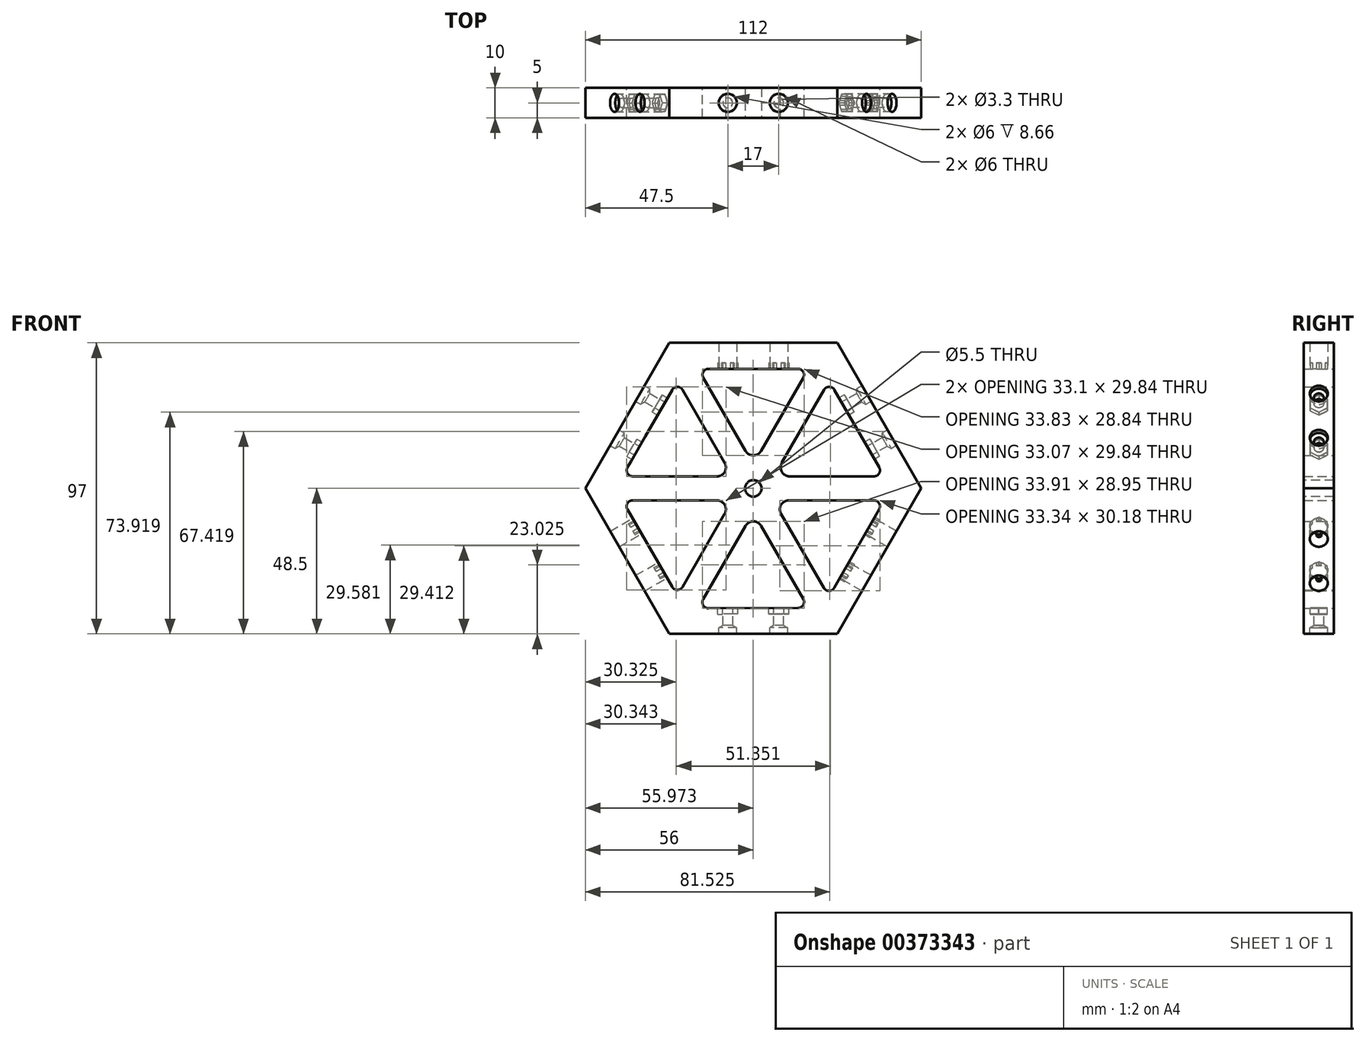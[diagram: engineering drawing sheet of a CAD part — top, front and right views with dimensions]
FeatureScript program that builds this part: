
annotation { "Feature Type Name" : "Feature", "Feature Type Description" : "" }
export const myFeature = defineFeature(function(context is Context, id is Id, definition is map)
    precondition{}
    {
        {
            var Q0;
            Q0=qCreatedBy(makeId("Front.planeOp"),FACE);
            var sketch = newSketch(context, id + "F0", { "sketchPlane" : qUnion([Q0])});
            skCircle(sketch, "E0.cCircle", {"center": v(0, 0) * mm, "radius": 56 * mm, "construction": true});
            skLineSegment(sketch, "E0.0", {"start": v(56, 0) * mm, "end": v(28, -48.5) * mm});
            skLineSegment(sketch, "E0.1", {"start": v(28, -48.5) * mm, "end": v(-28, -48.5) * mm});
            skLineSegment(sketch, "E0.2", {"start": v(-28, -48.5) * mm, "end": v(-56, 0) * mm});
            skLineSegment(sketch, "E0.3", {"start": v(-56, 0) * mm, "end": v(-28, 48.5) * mm});
            skLineSegment(sketch, "E0.4", {"start": v(-28, 48.5) * mm, "end": v(28, 48.5) * mm});
            skLineSegment(sketch, "E0.5", {"start": v(28, 48.5) * mm, "end": v(56, 0) * mm});
            skCircle(sketch, "E1.cCircle", {"center": v(0, 0) * mm, "radius": 46 * mm, "construction": true});
            skLineSegment(sketch, "E1.2", {"start": v(-27.04, -32.84) * mm, "end": v(-41.96, -7) * mm});
            skLineSegment(sketch, "E1.3", {"start": v(-36, 17.34) * mm, "end": v(-27.04, 32.84) * mm});
            skLineSegment(sketch, "E1.4", {"start": v(-14.92, 39.84) * mm, "end": v(14.92, 39.84) * mm});
            skPoint(sketch, "E2.newPointB", {"position": v(-46, 0) * mm});
            skPoint(sketch, "E3.visualSharp", {"position": v(-23, 39.84) * mm});
            skPoint(sketch, "E4.visualSharp", {"position": v(23, 39.84) * mm});
            skPoint(sketch, "E5.newPointA", {"position": v(46, 0) * mm});
            skPoint(sketch, "E6.visualSharp", {"position": v(23, -39.84) * mm});
            skLineSegment(sketch, "E7", {"start": v(-40.71, 9.07) * mm, "end": v(-41.92, 7) * mm});
            skPoint(sketch, "E8.visualSharp", {"position": v(-23, -39.84) * mm});
            skCircle(sketch, "E9", {"center": v(0, 0) * mm, "radius": 4 * mm});
            skLineSegment(sketch, "E10", {"start": v(-36, 17.34) * mm, "end": v(-40.71, 9.07) * mm});
            skLineSegment(sketch, "E11", {"start": v(41.93, -7) * mm, "end": v(26.97, -33.17) * mm});
            skPoint(sketch, "E12.startSnap0", {"position": v(-20.52, 10.54) * mm});
            skPoint(sketch, "E13", {"position": v(40.21, -10) * mm});
            skLineSegment(sketch, "E14", {"start": v(-12.12, 4) * mm, "end": v(-40.2, 4) * mm});
            skLineSegment(sketch, "E15", {"start": v(-12.12, -4) * mm, "end": v(-40.23, -4) * mm});
            skLineSegment(sketch, "E16", {"start": v(12.12, 4) * mm, "end": v(40.23, 4) * mm});
            skLineSegment(sketch, "E17", {"start": v(11.85, -4) * mm, "end": v(40.2, -4) * mm});
            skLineSegment(sketch, "E18", {"start": v(-2.6, 12.5) * mm, "end": v(-16.65, 36.84) * mm});
            skLineSegment(sketch, "E19", {"start": v(-9.53, 8.5) * mm, "end": v(-23.58, 32.84) * mm});
            skLineSegment(sketch, "E20", {"start": v(2.6, 12.5) * mm, "end": v(16.65, 36.84) * mm});
            skLineSegment(sketch, "E21", {"start": v(9.53, 8.5) * mm, "end": v(23.58, 32.84) * mm});
            skLineSegment(sketch, "E22", {"start": v(9.25, -8.5) * mm, "end": v(23.5, -33.18) * mm});
            skLineSegment(sketch, "E23", {"start": v(2.6, -12.5) * mm, "end": v(16.66, -36.85) * mm});
            skPoint(sketch, "E23.endSnap0", {"position": v(16.38, -39.84) * mm});
            skLineSegment(sketch, "E24", {"start": v(-2.6, -12.5) * mm, "end": v(-16.71, -36.95) * mm});
            skLineSegment(sketch, "E25", {"start": v(-9.53, -8.5) * mm, "end": v(-23.58, -32.84) * mm});
            skPoint(sketch, "E26.newPointA", {"position": v(-3.46, 2) * mm});
            skPoint(sketch, "E26.newPointB", {"position": v(3.46, 2) * mm});
            skArc(sketch, "E26.filletArc", {"start": v(-2.6, 12.5) * mm, "mid": v(0, 11) * mm, "end": v(2.6, 12.5) * mm});
            skArc(sketch, "E27.filletArc", {"start": v(9.53, 8.5) * mm, "mid": v(9.53, 5.5) * mm, "end": v(12.12, 4) * mm});
            skArc(sketch, "E28.filletArc", {"start": v(11.85, -4) * mm, "mid": v(9.25, -5.5) * mm, "end": v(9.25, -8.5) * mm});
            skArc(sketch, "E29.filletArc", {"start": v(2.6, -12.5) * mm, "mid": v(0, -11) * mm, "end": v(-2.6, -12.5) * mm});
            skPoint(sketch, "E30.newPointB", {"position": v(0, -4) * mm});
            skArc(sketch, "E30.filletArc", {"start": v(-9.53, -8.5) * mm, "mid": v(-9.53, -5.5) * mm, "end": v(-12.12, -4) * mm});
            skPoint(sketch, "E31.newPointA", {"position": v(0, 4) * mm});
            skArc(sketch, "E31.filletArc", {"start": v(-12.12, 4) * mm, "mid": v(-9.53, 5.5) * mm, "end": v(-9.53, 8.5) * mm});
            skArc(sketch, "E32.filletArc", {"start": v(16.65, 36.84) * mm, "mid": v(16.65, 38.84) * mm, "end": v(14.92, 39.84) * mm});
            skArc(sketch, "E33.filletArc", {"start": v(-23.58, 32.84) * mm, "mid": v(-25.3, 33.84) * mm, "end": v(-27.04, 32.84) * mm});
            skArc(sketch, "E34.filletArc", {"start": v(-14.92, 39.84) * mm, "mid": v(-16.65, 38.84) * mm, "end": v(-16.65, 36.84) * mm});
            skArc(sketch, "E35.filletArc", {"start": v(-41.92, 7) * mm, "mid": v(-41.92, 5) * mm, "end": v(-40.2, 4) * mm});
            skArc(sketch, "E36.filletArc", {"start": v(-40.23, -4) * mm, "mid": v(-41.96, -5) * mm, "end": v(-41.96, -7) * mm});
            skArc(sketch, "E37.filletArc", {"start": v(-27.04, -32.84) * mm, "mid": v(-25.3, -33.84) * mm, "end": v(-23.58, -32.84) * mm});
            skLineSegment(sketch, "E38", {"start": v(12.5, -39.84) * mm, "end": v(-14.97, -39.95) * mm});
            skArc(sketch, "E39.filletArc", {"start": v(-16.71, -36.95) * mm, "mid": v(-16.71, -38.95) * mm, "end": v(-14.97, -39.95) * mm});
            skLineSegment(sketch, "E40", {"start": v(-14.97, -39.95) * mm, "end": v(14.93, -39.85) * mm});
            skArc(sketch, "E41.filletArc", {"start": v(14.93, -39.85) * mm, "mid": v(16.66, -38.85) * mm, "end": v(16.66, -36.85) * mm});
            skArc(sketch, "E42.filletArc", {"start": v(23.5, -33.18) * mm, "mid": v(25.24, -34.18) * mm, "end": v(26.97, -33.17) * mm});
            skArc(sketch, "E43.filletArc", {"start": v(41.93, -7) * mm, "mid": v(41.93, -5) * mm, "end": v(40.2, -4) * mm});
            skArc(sketch, "E44.filletArc", {"start": v(40.23, 4) * mm, "mid": v(41.96, 5) * mm, "end": v(41.96, 7) * mm});
            skPoint(sketch, "E45.visualSharp", {"position": v(25.3, 35.84) * mm});
            skArc(sketch, "E45.filletArc", {"start": v(27.04, 32.84) * mm, "mid": v(25.3, 33.84) * mm, "end": v(23.58, 32.84) * mm});
            skLineSegment(sketch, "E46", {"start": v(27.04, 32.84) * mm, "end": v(41.96, 7) * mm});
            skSolve(sketch);
        }
        {
            var Q0;
            Q0=makeQuery(id+"F0.imprint","IMPRINT",FACE,{"disambiguationData":[TD([[makeQuery(id+"F0.imprint","IMPRINT",EDGE,{"derivedFrom":sQuery(id+"F0.wireOp",EDGE,"E0.0")}),-1.0]])]});
            var Q1;
            Q1=makeQuery(id+"F0.imprint","IMPRINT",FACE,{"disambiguationData":[TD([[makeQuery(id+"F0.imprint","IMPRINT",EDGE,{"derivedFrom":sQuery(id+"F0.wireOp",EDGE,"E9")}),1.0]])]});
            var Q2;
            Q2=makeQuery(id+"F0.imprint","IMPRINT",FACE,{"disambiguationData":[TD([[makeQuery(id+"F0.imprint","IMPRINT",EDGE,{"derivedFrom":sQuery(id+"F0.wireOp",EDGE,"qtYv5Qlg-lz4s-kEUD-Om88-7lSdra8USrlq")}),-1.0]])]});
            extrude(context, id + "F1", {"entities" : qUnion([Q0, Q1, Q2]), "depth" : 3 * mm});
        }
        {
            var Q0;
            Q0=qSketchRegion(id+"F0",true);
            var Q1;
            Q1=makeQuery(id+"F0.imprint","IMPRINT",FACE,{"disambiguationData":[TD([[makeQuery(id+"F0.imprint","IMPRINT",EDGE,{"derivedFrom":sQuery(id+"F0.wireOp",EDGE,"E9")}),1.0]])]});
            extrude(context, id + "F2", {"entities" : qUnion([Q0, Q1]), "operationType" : NewBodyOperationType.ADD, "depth" : 10 * mm});
        }
        {
            var Q0;
            {var subQ0=sQuery(id+"F0.wireOp",EDGE,"E0.1");Q0=makeQuery(id+"F2.boolean.opBoolean","MERGE",FACE,{"derivedFrom":[makeQuery(id+"F1.opExtrude","SWEPT_FACE",FACE,{"disambiguationData":[OSD([subQ0])]}),makeQuery(id+"F2.opExtrude","SWEPT_FACE",FACE,{"disambiguationData":[OSD([subQ0])]})]});}
            var sketch = newSketch(context, id + "F3", { "sketchPlane" : qUnion([Q0])});
            skPoint(sketch, "E47", {"position": v(-8.5, 5) * mm});
            skPoint(sketch, "E48", {"position": v(8.5, 5) * mm});
            skSolve(sketch);
        }
        {
            var Q0;
            {var subQ0=sQuery(id+"F0.wireOp",EDGE,"E0.0");Q0=makeQuery(id+"F2.boolean.opBoolean","MERGE",FACE,{"derivedFrom":[makeQuery(id+"F1.opExtrude","SWEPT_FACE",FACE,{"disambiguationData":[OSD([subQ0])]}),makeQuery(id+"F2.opExtrude","SWEPT_FACE",FACE,{"disambiguationData":[OSD([subQ0])]})]});}
            var sketch = newSketch(context, id + "F4", { "sketchPlane" : qUnion([Q0])});
            skPoint(sketch, "E49", {"position": v(-5, -8.5) * mm});
            skPoint(sketch, "E50", {"position": v(-5, 8.5) * mm});
            skSolve(sketch);
        }
        {
            var Q0;
            {var subQ0=sQuery(id+"F0.wireOp",EDGE,"E0.5");Q0=makeQuery(id+"F2.boolean.opBoolean","MERGE",FACE,{"derivedFrom":[makeQuery(id+"F1.opExtrude","SWEPT_FACE",FACE,{"disambiguationData":[OSD([subQ0])]}),makeQuery(id+"F2.opExtrude","SWEPT_FACE",FACE,{"disambiguationData":[OSD([subQ0])]})]});}
            var sketch = newSketch(context, id + "F5", { "sketchPlane" : qUnion([Q0])});
            skPoint(sketch, "E51", {"position": v(-5, -8.5) * mm});
            skPoint(sketch, "E52", {"position": v(-5, 8.5) * mm});
            skPoint(sketch, "E53.0.midPoint", {"position": v(-2.2, 8.5) * mm});
            skPoint(sketch, "E54.0.midPoint", {"position": v(-2.2, -8.5) * mm});
            skSolve(sketch);
        }
        {
            var Q0;
            {var subQ0=sQuery(id+"F0.wireOp",EDGE,"E0.3");Q0=makeQuery(id+"F2.boolean.opBoolean","MERGE",FACE,{"derivedFrom":[makeQuery(id+"F1.opExtrude","SWEPT_FACE",FACE,{"disambiguationData":[OSD([subQ0])]}),makeQuery(id+"F2.opExtrude","SWEPT_FACE",FACE,{"disambiguationData":[OSD([subQ0])]})]});}
            var sketch = newSketch(context, id + "F6", { "sketchPlane" : qUnion([Q0])});
            skPoint(sketch, "E55.endSnap0", {"position": v(5, 28) * mm});
            skPoint(sketch, "E56", {"position": v(5, 8.5) * mm});
            skPoint(sketch, "E57", {"position": v(5, -8.5) * mm});
            skSolve(sketch);
        }
        {
            var Q0;
            {var subQ0=sQuery(id+"F0.wireOp",EDGE,"E0.2");Q0=makeQuery(id+"F2.boolean.opBoolean","MERGE",FACE,{"derivedFrom":[makeQuery(id+"F1.opExtrude","SWEPT_FACE",FACE,{"disambiguationData":[OSD([subQ0])]}),makeQuery(id+"F2.opExtrude","SWEPT_FACE",FACE,{"disambiguationData":[OSD([subQ0])]})]});}
            var sketch = newSketch(context, id + "F7", { "sketchPlane" : qUnion([Q0])});
            skPoint(sketch, "E58", {"position": v(5, 8.5) * mm});
            skPoint(sketch, "E59", {"position": v(5, -8.5) * mm});
            skSolve(sketch);
        }
        {
            var Q0;
            Q0=sQuery(id+"F3.wireOp",VERTEX,"E47");
            var Q1;
            Q1=sQuery(id+"F3.wireOp",VERTEX,"E48");
            var Q2;
            Q2=makeQuery(id+"F1.opExtrude","SWEPT_BODY",BODY,{"disambiguationData":[OSD([sQuery(id+"F0.wireOp",EDGE,"E0.0"),sQuery(id+"F0.wireOp",EDGE,"E0.1"),sQuery(id+"F0.wireOp",EDGE,"E0.2"),sQuery(id+"F0.wireOp",EDGE,"E0.3"),sQuery(id+"F0.wireOp",EDGE,"E0.4"),sQuery(id+"F0.wireOp",EDGE,"E0.5"),sQuery(id+"F0.wireOp",EDGE,"E1.0"),sQuery(id+"F0.wireOp",EDGE,"E1.1"),sQuery(id+"F0.wireOp",EDGE,"E1.2"),sQuery(id+"F0.wireOp",EDGE,"E1.3"),sQuery(id+"F0.wireOp",EDGE,"E1.4"),sQuery(id+"F0.wireOp",EDGE,"E1.5"),sQuery(id+"F0.wireOp",EDGE,"qtYv5Qlg-lz4s-kEUD-Om88-7lSdra8USrlq"),sQuery(id+"F0.wireOp",EDGE,"2QYJyqNU-itui-Txcm-ziau-iXFr887Gd9CH"),sQuery(id+"F0.wireOp",EDGE,"YySKseKW-3tVR-XM2i-sfbE-A3hUb2wOsWk8"),sQuery(id+"F0.wireOp",EDGE,"Lxbxjq0N-10Ww-tbja-2Tz2-jBNBnu8PBPbP"),sQuery(id+"F0.wireOp",EDGE,"vIwuUKl2-2Kem-1Jnu-9PgQ-0QrErVIrz4Um"),sQuery(id+"F0.wireOp",EDGE,"fKHDwvwM-en0X-JEBE-N4jP-jXe72wWVmmUP"),sQuery(id+"F0.wireOp",EDGE,"E2.filletArc"),sQuery(id+"F0.wireOp",EDGE,"E3.filletArc"),sQuery(id+"F0.wireOp",EDGE,"E4.filletArc"),sQuery(id+"F0.wireOp",EDGE,"E5.filletArc"),sQuery(id+"F0.wireOp",EDGE,"E6.filletArc"),sQuery(id+"F0.wireOp",EDGE,"f75670f9-2a15-46ef-bb35-30587241fc96.filletArc"),sQuery(id+"F0.wireOp",EDGE,"c95b92e2-db18-4474-b396-5f44c590ad15.filletArc"),sQuery(id+"F0.wireOp",EDGE,"f16d8751-d18c-4831-acbc-1a13bea7c6bc.filletArc"),sQuery(id+"F0.wireOp",EDGE,"ea1bd330-e894-4266-8a44-9dcd888b044d.filletArc"),sQuery(id+"F0.wireOp",EDGE,"E7"),sQuery(id+"F0.wireOp",EDGE,"mCzg0sP5-OklU-KqC0-8pOI-dyTgrQixTGRZ"),sQuery(id+"F0.wireOp",EDGE,"WcAi2qTU-oJVa-IYYN-hlim-nuIIgn7LXuB4"),sQuery(id+"F0.wireOp",EDGE,"d29a9537-46ff-4a88-b732-ec67f0ea45bd.filletArc"),sQuery(id+"F0.wireOp",EDGE,"ad75a4ee-e5a6-4fa7-b8b8-94f4a8825bbc.filletArc"),sQuery(id+"F0.wireOp",EDGE,"6ff16504-1f9c-458d-bf07-aac5f5830d14.filletArc"),sQuery(id+"F0.wireOp",EDGE,"b49fe1c4-a771-4eee-9138-79ecde32758b.filletArc"),sQuery(id+"F0.wireOp",EDGE,"E8.filletArc"),sQuery(id+"F0.wireOp",EDGE,"780f9540-5b47-44f2-a996-e532c960a919.filletArc")])]});
            hole(context, id + "F8", {"style" : HoleStyle.SIMPLE, "endStyle" : HoleEndStyle.BLIND, "holeDiameter" : 6 * mm, "holeDepth" : 2 * mm, "tappedDepth" : 12 * mm, "tapClearance" : 3, "locations" : qUnion([Q0, Q1]), "scope" : qUnion([Q2])});
        }
        {
            var Q0;
            Q0=sQuery(id+"F3.wireOp",VERTEX,"E47");
            var Q1;
            Q1=sQuery(id+"F3.wireOp",VERTEX,"E48");
            var Q2;
            Q2=makeQuery(id+"F1.opExtrude","SWEPT_BODY",BODY,{"disambiguationData":[OSD([sQuery(id+"F0.wireOp",EDGE,"E0.0"),sQuery(id+"F0.wireOp",EDGE,"E0.1"),sQuery(id+"F0.wireOp",EDGE,"E0.2"),sQuery(id+"F0.wireOp",EDGE,"E0.3"),sQuery(id+"F0.wireOp",EDGE,"E0.4"),sQuery(id+"F0.wireOp",EDGE,"E0.5"),sQuery(id+"F0.wireOp",EDGE,"E1.0"),sQuery(id+"F0.wireOp",EDGE,"E1.1"),sQuery(id+"F0.wireOp",EDGE,"E1.2"),sQuery(id+"F0.wireOp",EDGE,"E1.3"),sQuery(id+"F0.wireOp",EDGE,"E1.4"),sQuery(id+"F0.wireOp",EDGE,"E1.5"),sQuery(id+"F0.wireOp",EDGE,"qtYv5Qlg-lz4s-kEUD-Om88-7lSdra8USrlq"),sQuery(id+"F0.wireOp",EDGE,"2QYJyqNU-itui-Txcm-ziau-iXFr887Gd9CH"),sQuery(id+"F0.wireOp",EDGE,"YySKseKW-3tVR-XM2i-sfbE-A3hUb2wOsWk8"),sQuery(id+"F0.wireOp",EDGE,"Lxbxjq0N-10Ww-tbja-2Tz2-jBNBnu8PBPbP"),sQuery(id+"F0.wireOp",EDGE,"vIwuUKl2-2Kem-1Jnu-9PgQ-0QrErVIrz4Um"),sQuery(id+"F0.wireOp",EDGE,"fKHDwvwM-en0X-JEBE-N4jP-jXe72wWVmmUP"),sQuery(id+"F0.wireOp",EDGE,"E2.filletArc"),sQuery(id+"F0.wireOp",EDGE,"E3.filletArc"),sQuery(id+"F0.wireOp",EDGE,"E4.filletArc"),sQuery(id+"F0.wireOp",EDGE,"E5.filletArc"),sQuery(id+"F0.wireOp",EDGE,"E6.filletArc"),sQuery(id+"F0.wireOp",EDGE,"f75670f9-2a15-46ef-bb35-30587241fc96.filletArc"),sQuery(id+"F0.wireOp",EDGE,"c95b92e2-db18-4474-b396-5f44c590ad15.filletArc"),sQuery(id+"F0.wireOp",EDGE,"f16d8751-d18c-4831-acbc-1a13bea7c6bc.filletArc"),sQuery(id+"F0.wireOp",EDGE,"ea1bd330-e894-4266-8a44-9dcd888b044d.filletArc"),sQuery(id+"F0.wireOp",EDGE,"E7"),sQuery(id+"F0.wireOp",EDGE,"mCzg0sP5-OklU-KqC0-8pOI-dyTgrQixTGRZ"),sQuery(id+"F0.wireOp",EDGE,"WcAi2qTU-oJVa-IYYN-hlim-nuIIgn7LXuB4"),sQuery(id+"F0.wireOp",EDGE,"d29a9537-46ff-4a88-b732-ec67f0ea45bd.filletArc"),sQuery(id+"F0.wireOp",EDGE,"ad75a4ee-e5a6-4fa7-b8b8-94f4a8825bbc.filletArc"),sQuery(id+"F0.wireOp",EDGE,"6ff16504-1f9c-458d-bf07-aac5f5830d14.filletArc"),sQuery(id+"F0.wireOp",EDGE,"b49fe1c4-a771-4eee-9138-79ecde32758b.filletArc"),sQuery(id+"F0.wireOp",EDGE,"E8.filletArc"),sQuery(id+"F0.wireOp",EDGE,"780f9540-5b47-44f2-a996-e532c960a919.filletArc")])]});
            hole(context, id + "F9", {"style" : HoleStyle.SIMPLE, "endStyle" : HoleEndStyle.BLIND, "standardTappedOrClearance" : lookupTablePath({ "standard" : "ISO", "fit" : "Normal", "size" : "M3", "type" : "Clearance" }), "standardBlindInLast" : lookupTablePath({ "fit" : "Standard", "standard" : "ISO", "size" : "M3", "type" : "Clearance" }), "holeDiameter" : 3.3 * mm, "holeDepth" : 13.5 * mm, "tappedDepth" : 12 * mm, "tapClearance" : 3, "locations" : qUnion([Q0, Q1]), "scope" : qUnion([Q2])});
        }
        {
            var Q0;
            Q0=sQuery(id+"F4.wireOp",VERTEX,"E49");
            var Q1;
            Q1=sQuery(id+"F4.wireOp",VERTEX,"E50");
            var Q2;
            Q2=makeQuery(id+"F1.opExtrude","SWEPT_BODY",BODY,{"disambiguationData":[OSD([sQuery(id+"F0.wireOp",EDGE,"E0.0"),sQuery(id+"F0.wireOp",EDGE,"E0.1"),sQuery(id+"F0.wireOp",EDGE,"E0.2"),sQuery(id+"F0.wireOp",EDGE,"E0.3"),sQuery(id+"F0.wireOp",EDGE,"E0.4"),sQuery(id+"F0.wireOp",EDGE,"E0.5"),sQuery(id+"F0.wireOp",EDGE,"E1.0"),sQuery(id+"F0.wireOp",EDGE,"E1.1"),sQuery(id+"F0.wireOp",EDGE,"E1.2"),sQuery(id+"F0.wireOp",EDGE,"E1.3"),sQuery(id+"F0.wireOp",EDGE,"E1.4"),sQuery(id+"F0.wireOp",EDGE,"E1.5"),sQuery(id+"F0.wireOp",EDGE,"qtYv5Qlg-lz4s-kEUD-Om88-7lSdra8USrlq"),sQuery(id+"F0.wireOp",EDGE,"2QYJyqNU-itui-Txcm-ziau-iXFr887Gd9CH"),sQuery(id+"F0.wireOp",EDGE,"YySKseKW-3tVR-XM2i-sfbE-A3hUb2wOsWk8"),sQuery(id+"F0.wireOp",EDGE,"Lxbxjq0N-10Ww-tbja-2Tz2-jBNBnu8PBPbP"),sQuery(id+"F0.wireOp",EDGE,"vIwuUKl2-2Kem-1Jnu-9PgQ-0QrErVIrz4Um"),sQuery(id+"F0.wireOp",EDGE,"fKHDwvwM-en0X-JEBE-N4jP-jXe72wWVmmUP"),sQuery(id+"F0.wireOp",EDGE,"E2.filletArc"),sQuery(id+"F0.wireOp",EDGE,"E3.filletArc"),sQuery(id+"F0.wireOp",EDGE,"E4.filletArc"),sQuery(id+"F0.wireOp",EDGE,"E5.filletArc"),sQuery(id+"F0.wireOp",EDGE,"E6.filletArc"),sQuery(id+"F0.wireOp",EDGE,"f75670f9-2a15-46ef-bb35-30587241fc96.filletArc"),sQuery(id+"F0.wireOp",EDGE,"c95b92e2-db18-4474-b396-5f44c590ad15.filletArc"),sQuery(id+"F0.wireOp",EDGE,"f16d8751-d18c-4831-acbc-1a13bea7c6bc.filletArc"),sQuery(id+"F0.wireOp",EDGE,"ea1bd330-e894-4266-8a44-9dcd888b044d.filletArc"),sQuery(id+"F0.wireOp",EDGE,"E7"),sQuery(id+"F0.wireOp",EDGE,"mCzg0sP5-OklU-KqC0-8pOI-dyTgrQixTGRZ"),sQuery(id+"F0.wireOp",EDGE,"WcAi2qTU-oJVa-IYYN-hlim-nuIIgn7LXuB4"),sQuery(id+"F0.wireOp",EDGE,"d29a9537-46ff-4a88-b732-ec67f0ea45bd.filletArc"),sQuery(id+"F0.wireOp",EDGE,"ad75a4ee-e5a6-4fa7-b8b8-94f4a8825bbc.filletArc"),sQuery(id+"F0.wireOp",EDGE,"6ff16504-1f9c-458d-bf07-aac5f5830d14.filletArc"),sQuery(id+"F0.wireOp",EDGE,"b49fe1c4-a771-4eee-9138-79ecde32758b.filletArc"),sQuery(id+"F0.wireOp",EDGE,"E8.filletArc"),sQuery(id+"F0.wireOp",EDGE,"780f9540-5b47-44f2-a996-e532c960a919.filletArc")])]});
            hole(context, id + "F10", {"style" : HoleStyle.SIMPLE, "endStyle" : HoleEndStyle.BLIND, "standardTappedOrClearance" : lookupTablePath({ "standard" : "ISO", "fit" : "Normal", "size" : "M3", "type" : "Clearance" }), "standardBlindInLast" : lookupTablePath({ "fit" : "Standard", "standard" : "ISO", "size" : "M3", "type" : "Clearance" }), "holeDiameter" : 3.3 * mm, "holeDepth" : 13.5 * mm, "tappedDepth" : 12 * mm, "tapClearance" : 3, "locations" : qUnion([Q0, Q1]), "scope" : qUnion([Q2])});
        }
        {
            var Q0;
            Q0=sQuery(id+"F4.wireOp",VERTEX,"E49");
            var Q1;
            Q1=sQuery(id+"F4.wireOp",VERTEX,"E50");
            var Q2;
            Q2=makeQuery(id+"F1.opExtrude","SWEPT_BODY",BODY,{"disambiguationData":[OSD([sQuery(id+"F0.wireOp",EDGE,"E0.0"),sQuery(id+"F0.wireOp",EDGE,"E0.1"),sQuery(id+"F0.wireOp",EDGE,"E0.2"),sQuery(id+"F0.wireOp",EDGE,"E0.3"),sQuery(id+"F0.wireOp",EDGE,"E0.4"),sQuery(id+"F0.wireOp",EDGE,"E0.5"),sQuery(id+"F0.wireOp",EDGE,"E1.0"),sQuery(id+"F0.wireOp",EDGE,"E1.1"),sQuery(id+"F0.wireOp",EDGE,"E1.2"),sQuery(id+"F0.wireOp",EDGE,"E1.3"),sQuery(id+"F0.wireOp",EDGE,"E1.4"),sQuery(id+"F0.wireOp",EDGE,"E1.5"),sQuery(id+"F0.wireOp",EDGE,"qtYv5Qlg-lz4s-kEUD-Om88-7lSdra8USrlq"),sQuery(id+"F0.wireOp",EDGE,"2QYJyqNU-itui-Txcm-ziau-iXFr887Gd9CH"),sQuery(id+"F0.wireOp",EDGE,"YySKseKW-3tVR-XM2i-sfbE-A3hUb2wOsWk8"),sQuery(id+"F0.wireOp",EDGE,"Lxbxjq0N-10Ww-tbja-2Tz2-jBNBnu8PBPbP"),sQuery(id+"F0.wireOp",EDGE,"vIwuUKl2-2Kem-1Jnu-9PgQ-0QrErVIrz4Um"),sQuery(id+"F0.wireOp",EDGE,"fKHDwvwM-en0X-JEBE-N4jP-jXe72wWVmmUP"),sQuery(id+"F0.wireOp",EDGE,"E2.filletArc"),sQuery(id+"F0.wireOp",EDGE,"E3.filletArc"),sQuery(id+"F0.wireOp",EDGE,"E4.filletArc"),sQuery(id+"F0.wireOp",EDGE,"E5.filletArc"),sQuery(id+"F0.wireOp",EDGE,"E6.filletArc"),sQuery(id+"F0.wireOp",EDGE,"f75670f9-2a15-46ef-bb35-30587241fc96.filletArc"),sQuery(id+"F0.wireOp",EDGE,"c95b92e2-db18-4474-b396-5f44c590ad15.filletArc"),sQuery(id+"F0.wireOp",EDGE,"f16d8751-d18c-4831-acbc-1a13bea7c6bc.filletArc"),sQuery(id+"F0.wireOp",EDGE,"ea1bd330-e894-4266-8a44-9dcd888b044d.filletArc"),sQuery(id+"F0.wireOp",EDGE,"E7"),sQuery(id+"F0.wireOp",EDGE,"mCzg0sP5-OklU-KqC0-8pOI-dyTgrQixTGRZ"),sQuery(id+"F0.wireOp",EDGE,"WcAi2qTU-oJVa-IYYN-hlim-nuIIgn7LXuB4"),sQuery(id+"F0.wireOp",EDGE,"d29a9537-46ff-4a88-b732-ec67f0ea45bd.filletArc"),sQuery(id+"F0.wireOp",EDGE,"ad75a4ee-e5a6-4fa7-b8b8-94f4a8825bbc.filletArc"),sQuery(id+"F0.wireOp",EDGE,"6ff16504-1f9c-458d-bf07-aac5f5830d14.filletArc"),sQuery(id+"F0.wireOp",EDGE,"b49fe1c4-a771-4eee-9138-79ecde32758b.filletArc"),sQuery(id+"F0.wireOp",EDGE,"E8.filletArc"),sQuery(id+"F0.wireOp",EDGE,"780f9540-5b47-44f2-a996-e532c960a919.filletArc")])]});
            hole(context, id + "F11", {"style" : HoleStyle.SIMPLE, "endStyle" : HoleEndStyle.BLIND, "holeDiameter" : 6 * mm, "holeDepth" : 2 * mm, "tappedDepth" : 12 * mm, "tapClearance" : 3, "locations" : qUnion([Q0, Q1]), "scope" : qUnion([Q2])});
        }
        {
            var Q0;
            Q0=sQuery(id+"F5.wireOp",VERTEX,"E51");
            var Q1;
            Q1=sQuery(id+"F5.wireOp",VERTEX,"E52");
            var Q2;
            Q2=makeQuery(id+"F1.opExtrude","SWEPT_BODY",BODY,{"disambiguationData":[OSD([sQuery(id+"F0.wireOp",EDGE,"E0.0"),sQuery(id+"F0.wireOp",EDGE,"E0.1"),sQuery(id+"F0.wireOp",EDGE,"E0.2"),sQuery(id+"F0.wireOp",EDGE,"E0.3"),sQuery(id+"F0.wireOp",EDGE,"E0.4"),sQuery(id+"F0.wireOp",EDGE,"E0.5"),sQuery(id+"F0.wireOp",EDGE,"E1.0"),sQuery(id+"F0.wireOp",EDGE,"E1.1"),sQuery(id+"F0.wireOp",EDGE,"E1.2"),sQuery(id+"F0.wireOp",EDGE,"E1.3"),sQuery(id+"F0.wireOp",EDGE,"E1.4"),sQuery(id+"F0.wireOp",EDGE,"E1.5"),sQuery(id+"F0.wireOp",EDGE,"qtYv5Qlg-lz4s-kEUD-Om88-7lSdra8USrlq"),sQuery(id+"F0.wireOp",EDGE,"2QYJyqNU-itui-Txcm-ziau-iXFr887Gd9CH"),sQuery(id+"F0.wireOp",EDGE,"YySKseKW-3tVR-XM2i-sfbE-A3hUb2wOsWk8"),sQuery(id+"F0.wireOp",EDGE,"Lxbxjq0N-10Ww-tbja-2Tz2-jBNBnu8PBPbP"),sQuery(id+"F0.wireOp",EDGE,"vIwuUKl2-2Kem-1Jnu-9PgQ-0QrErVIrz4Um"),sQuery(id+"F0.wireOp",EDGE,"fKHDwvwM-en0X-JEBE-N4jP-jXe72wWVmmUP"),sQuery(id+"F0.wireOp",EDGE,"E2.filletArc"),sQuery(id+"F0.wireOp",EDGE,"E3.filletArc"),sQuery(id+"F0.wireOp",EDGE,"E4.filletArc"),sQuery(id+"F0.wireOp",EDGE,"E5.filletArc"),sQuery(id+"F0.wireOp",EDGE,"E6.filletArc"),sQuery(id+"F0.wireOp",EDGE,"f75670f9-2a15-46ef-bb35-30587241fc96.filletArc"),sQuery(id+"F0.wireOp",EDGE,"c95b92e2-db18-4474-b396-5f44c590ad15.filletArc"),sQuery(id+"F0.wireOp",EDGE,"f16d8751-d18c-4831-acbc-1a13bea7c6bc.filletArc"),sQuery(id+"F0.wireOp",EDGE,"ea1bd330-e894-4266-8a44-9dcd888b044d.filletArc"),sQuery(id+"F0.wireOp",EDGE,"E7"),sQuery(id+"F0.wireOp",EDGE,"mCzg0sP5-OklU-KqC0-8pOI-dyTgrQixTGRZ"),sQuery(id+"F0.wireOp",EDGE,"WcAi2qTU-oJVa-IYYN-hlim-nuIIgn7LXuB4"),sQuery(id+"F0.wireOp",EDGE,"d29a9537-46ff-4a88-b732-ec67f0ea45bd.filletArc"),sQuery(id+"F0.wireOp",EDGE,"ad75a4ee-e5a6-4fa7-b8b8-94f4a8825bbc.filletArc"),sQuery(id+"F0.wireOp",EDGE,"6ff16504-1f9c-458d-bf07-aac5f5830d14.filletArc"),sQuery(id+"F0.wireOp",EDGE,"b49fe1c4-a771-4eee-9138-79ecde32758b.filletArc"),sQuery(id+"F0.wireOp",EDGE,"E8.filletArc"),sQuery(id+"F0.wireOp",EDGE,"780f9540-5b47-44f2-a996-e532c960a919.filletArc")])]});
            hole(context, id + "F12", {"style" : HoleStyle.SIMPLE, "endStyle" : HoleEndStyle.BLIND, "holeDiameter" : 6 * mm, "holeDepth" : 2 * mm, "tappedDepth" : 12 * mm, "tapClearance" : 3, "locations" : qUnion([Q0, Q1]), "scope" : qUnion([Q2])});
        }
        {
            var Q0;
            Q0=sQuery(id+"F5.wireOp",VERTEX,"E51");
            var Q1;
            Q1=sQuery(id+"F5.wireOp",VERTEX,"E52");
            var Q2;
            Q2=makeQuery(id+"F1.opExtrude","SWEPT_BODY",BODY,{"disambiguationData":[OSD([sQuery(id+"F0.wireOp",EDGE,"E0.0"),sQuery(id+"F0.wireOp",EDGE,"E0.1"),sQuery(id+"F0.wireOp",EDGE,"E0.2"),sQuery(id+"F0.wireOp",EDGE,"E0.3"),sQuery(id+"F0.wireOp",EDGE,"E0.4"),sQuery(id+"F0.wireOp",EDGE,"E0.5"),sQuery(id+"F0.wireOp",EDGE,"E1.0"),sQuery(id+"F0.wireOp",EDGE,"E1.1"),sQuery(id+"F0.wireOp",EDGE,"E1.2"),sQuery(id+"F0.wireOp",EDGE,"E1.3"),sQuery(id+"F0.wireOp",EDGE,"E1.4"),sQuery(id+"F0.wireOp",EDGE,"E1.5"),sQuery(id+"F0.wireOp",EDGE,"qtYv5Qlg-lz4s-kEUD-Om88-7lSdra8USrlq"),sQuery(id+"F0.wireOp",EDGE,"2QYJyqNU-itui-Txcm-ziau-iXFr887Gd9CH"),sQuery(id+"F0.wireOp",EDGE,"YySKseKW-3tVR-XM2i-sfbE-A3hUb2wOsWk8"),sQuery(id+"F0.wireOp",EDGE,"Lxbxjq0N-10Ww-tbja-2Tz2-jBNBnu8PBPbP"),sQuery(id+"F0.wireOp",EDGE,"vIwuUKl2-2Kem-1Jnu-9PgQ-0QrErVIrz4Um"),sQuery(id+"F0.wireOp",EDGE,"fKHDwvwM-en0X-JEBE-N4jP-jXe72wWVmmUP"),sQuery(id+"F0.wireOp",EDGE,"E2.filletArc"),sQuery(id+"F0.wireOp",EDGE,"E3.filletArc"),sQuery(id+"F0.wireOp",EDGE,"E4.filletArc"),sQuery(id+"F0.wireOp",EDGE,"E5.filletArc"),sQuery(id+"F0.wireOp",EDGE,"E6.filletArc"),sQuery(id+"F0.wireOp",EDGE,"f75670f9-2a15-46ef-bb35-30587241fc96.filletArc"),sQuery(id+"F0.wireOp",EDGE,"c95b92e2-db18-4474-b396-5f44c590ad15.filletArc"),sQuery(id+"F0.wireOp",EDGE,"f16d8751-d18c-4831-acbc-1a13bea7c6bc.filletArc"),sQuery(id+"F0.wireOp",EDGE,"ea1bd330-e894-4266-8a44-9dcd888b044d.filletArc"),sQuery(id+"F0.wireOp",EDGE,"E7"),sQuery(id+"F0.wireOp",EDGE,"mCzg0sP5-OklU-KqC0-8pOI-dyTgrQixTGRZ"),sQuery(id+"F0.wireOp",EDGE,"WcAi2qTU-oJVa-IYYN-hlim-nuIIgn7LXuB4"),sQuery(id+"F0.wireOp",EDGE,"d29a9537-46ff-4a88-b732-ec67f0ea45bd.filletArc"),sQuery(id+"F0.wireOp",EDGE,"ad75a4ee-e5a6-4fa7-b8b8-94f4a8825bbc.filletArc"),sQuery(id+"F0.wireOp",EDGE,"6ff16504-1f9c-458d-bf07-aac5f5830d14.filletArc"),sQuery(id+"F0.wireOp",EDGE,"b49fe1c4-a771-4eee-9138-79ecde32758b.filletArc"),sQuery(id+"F0.wireOp",EDGE,"E8.filletArc"),sQuery(id+"F0.wireOp",EDGE,"780f9540-5b47-44f2-a996-e532c960a919.filletArc")])]});
            hole(context, id + "F13", {"style" : HoleStyle.SIMPLE, "endStyle" : HoleEndStyle.BLIND, "standardTappedOrClearance" : lookupTablePath({ "standard" : "ISO", "fit" : "Normal", "size" : "M3", "type" : "Clearance" }), "standardBlindInLast" : lookupTablePath({ "fit" : "Standard", "standard" : "ISO", "size" : "M3", "type" : "Clearance" }), "holeDiameter" : 3.3 * mm, "holeDepth" : 13.5 * mm, "tappedDepth" : 12 * mm, "tapClearance" : 3, "locations" : qUnion([Q0, Q1]), "scope" : qUnion([Q2])});
        }
        {
            var Q0;
            {var subQ0=sQuery(id+"F0.wireOp",EDGE,"E0.4");Q0=makeQuery(id+"F2.boolean.opBoolean","MERGE",FACE,{"derivedFrom":[makeQuery(id+"F1.opExtrude","SWEPT_FACE",FACE,{"disambiguationData":[OSD([subQ0])]}),makeQuery(id+"F2.opExtrude","SWEPT_FACE",FACE,{"disambiguationData":[OSD([subQ0])]})]});}
            var sketch = newSketch(context, id + "F14", { "sketchPlane" : qUnion([Q0])});
            skPoint(sketch, "E60", {"position": v(8.5, -5) * mm});
            skPoint(sketch, "E61", {"position": v(-8.5, -5) * mm});
            skSolve(sketch);
        }
        {
            var Q0;
            Q0=sQuery(id+"F14.wireOp",VERTEX,"E60");
            var Q1;
            Q1=sQuery(id+"F14.wireOp",VERTEX,"E61");
            var Q2;
            Q2=makeQuery(id+"F1.opExtrude","SWEPT_BODY",BODY,{"disambiguationData":[OSD([sQuery(id+"F0.wireOp",EDGE,"E0.0"),sQuery(id+"F0.wireOp",EDGE,"E0.1"),sQuery(id+"F0.wireOp",EDGE,"E0.2"),sQuery(id+"F0.wireOp",EDGE,"E0.3"),sQuery(id+"F0.wireOp",EDGE,"E0.4"),sQuery(id+"F0.wireOp",EDGE,"E0.5"),sQuery(id+"F0.wireOp",EDGE,"E1.0"),sQuery(id+"F0.wireOp",EDGE,"E1.1"),sQuery(id+"F0.wireOp",EDGE,"E1.2"),sQuery(id+"F0.wireOp",EDGE,"E1.3"),sQuery(id+"F0.wireOp",EDGE,"E1.4"),sQuery(id+"F0.wireOp",EDGE,"E1.5"),sQuery(id+"F0.wireOp",EDGE,"qtYv5Qlg-lz4s-kEUD-Om88-7lSdra8USrlq"),sQuery(id+"F0.wireOp",EDGE,"2QYJyqNU-itui-Txcm-ziau-iXFr887Gd9CH"),sQuery(id+"F0.wireOp",EDGE,"YySKseKW-3tVR-XM2i-sfbE-A3hUb2wOsWk8"),sQuery(id+"F0.wireOp",EDGE,"Lxbxjq0N-10Ww-tbja-2Tz2-jBNBnu8PBPbP"),sQuery(id+"F0.wireOp",EDGE,"vIwuUKl2-2Kem-1Jnu-9PgQ-0QrErVIrz4Um"),sQuery(id+"F0.wireOp",EDGE,"fKHDwvwM-en0X-JEBE-N4jP-jXe72wWVmmUP"),sQuery(id+"F0.wireOp",EDGE,"E2.filletArc"),sQuery(id+"F0.wireOp",EDGE,"E3.filletArc"),sQuery(id+"F0.wireOp",EDGE,"E4.filletArc"),sQuery(id+"F0.wireOp",EDGE,"E5.filletArc"),sQuery(id+"F0.wireOp",EDGE,"E6.filletArc"),sQuery(id+"F0.wireOp",EDGE,"f75670f9-2a15-46ef-bb35-30587241fc96.filletArc"),sQuery(id+"F0.wireOp",EDGE,"c95b92e2-db18-4474-b396-5f44c590ad15.filletArc"),sQuery(id+"F0.wireOp",EDGE,"f16d8751-d18c-4831-acbc-1a13bea7c6bc.filletArc"),sQuery(id+"F0.wireOp",EDGE,"ea1bd330-e894-4266-8a44-9dcd888b044d.filletArc"),sQuery(id+"F0.wireOp",EDGE,"E7"),sQuery(id+"F0.wireOp",EDGE,"mCzg0sP5-OklU-KqC0-8pOI-dyTgrQixTGRZ"),sQuery(id+"F0.wireOp",EDGE,"WcAi2qTU-oJVa-IYYN-hlim-nuIIgn7LXuB4"),sQuery(id+"F0.wireOp",EDGE,"d29a9537-46ff-4a88-b732-ec67f0ea45bd.filletArc"),sQuery(id+"F0.wireOp",EDGE,"ad75a4ee-e5a6-4fa7-b8b8-94f4a8825bbc.filletArc"),sQuery(id+"F0.wireOp",EDGE,"6ff16504-1f9c-458d-bf07-aac5f5830d14.filletArc"),sQuery(id+"F0.wireOp",EDGE,"b49fe1c4-a771-4eee-9138-79ecde32758b.filletArc"),sQuery(id+"F0.wireOp",EDGE,"E8.filletArc"),sQuery(id+"F0.wireOp",EDGE,"780f9540-5b47-44f2-a996-e532c960a919.filletArc")])]});
            hole(context, id + "F15", {"style" : HoleStyle.SIMPLE, "endStyle" : HoleEndStyle.BLIND, "standardTappedOrClearance" : lookupTablePath({ "standard" : "ISO", "fit" : "Normal", "size" : "M3", "type" : "Clearance" }), "standardBlindInLast" : lookupTablePath({ "fit" : "Standard", "standard" : "ISO", "size" : "M3", "type" : "Clearance" }), "holeDiameter" : 3.3 * mm, "holeDepth" : 13.5 * mm, "tappedDepth" : 12 * mm, "tapClearance" : 3, "locations" : qUnion([Q0, Q1]), "scope" : qUnion([Q2])});
        }
        {
            var Q0;
            Q0=sQuery(id+"F14.wireOp",VERTEX,"E60");
            var Q1;
            Q1=sQuery(id+"F14.wireOp",VERTEX,"E61");
            var Q2;
            Q2=makeQuery(id+"F1.opExtrude","SWEPT_BODY",BODY,{"disambiguationData":[OSD([sQuery(id+"F0.wireOp",EDGE,"E0.0"),sQuery(id+"F0.wireOp",EDGE,"E0.1"),sQuery(id+"F0.wireOp",EDGE,"E0.2"),sQuery(id+"F0.wireOp",EDGE,"E0.3"),sQuery(id+"F0.wireOp",EDGE,"E0.4"),sQuery(id+"F0.wireOp",EDGE,"E0.5"),sQuery(id+"F0.wireOp",EDGE,"E1.0"),sQuery(id+"F0.wireOp",EDGE,"E1.1"),sQuery(id+"F0.wireOp",EDGE,"E1.2"),sQuery(id+"F0.wireOp",EDGE,"E1.3"),sQuery(id+"F0.wireOp",EDGE,"E1.4"),sQuery(id+"F0.wireOp",EDGE,"E1.5"),sQuery(id+"F0.wireOp",EDGE,"qtYv5Qlg-lz4s-kEUD-Om88-7lSdra8USrlq"),sQuery(id+"F0.wireOp",EDGE,"2QYJyqNU-itui-Txcm-ziau-iXFr887Gd9CH"),sQuery(id+"F0.wireOp",EDGE,"YySKseKW-3tVR-XM2i-sfbE-A3hUb2wOsWk8"),sQuery(id+"F0.wireOp",EDGE,"Lxbxjq0N-10Ww-tbja-2Tz2-jBNBnu8PBPbP"),sQuery(id+"F0.wireOp",EDGE,"vIwuUKl2-2Kem-1Jnu-9PgQ-0QrErVIrz4Um"),sQuery(id+"F0.wireOp",EDGE,"fKHDwvwM-en0X-JEBE-N4jP-jXe72wWVmmUP"),sQuery(id+"F0.wireOp",EDGE,"E2.filletArc"),sQuery(id+"F0.wireOp",EDGE,"E3.filletArc"),sQuery(id+"F0.wireOp",EDGE,"E4.filletArc"),sQuery(id+"F0.wireOp",EDGE,"E5.filletArc"),sQuery(id+"F0.wireOp",EDGE,"E6.filletArc"),sQuery(id+"F0.wireOp",EDGE,"f75670f9-2a15-46ef-bb35-30587241fc96.filletArc"),sQuery(id+"F0.wireOp",EDGE,"c95b92e2-db18-4474-b396-5f44c590ad15.filletArc"),sQuery(id+"F0.wireOp",EDGE,"f16d8751-d18c-4831-acbc-1a13bea7c6bc.filletArc"),sQuery(id+"F0.wireOp",EDGE,"ea1bd330-e894-4266-8a44-9dcd888b044d.filletArc"),sQuery(id+"F0.wireOp",EDGE,"E7"),sQuery(id+"F0.wireOp",EDGE,"mCzg0sP5-OklU-KqC0-8pOI-dyTgrQixTGRZ"),sQuery(id+"F0.wireOp",EDGE,"WcAi2qTU-oJVa-IYYN-hlim-nuIIgn7LXuB4"),sQuery(id+"F0.wireOp",EDGE,"d29a9537-46ff-4a88-b732-ec67f0ea45bd.filletArc"),sQuery(id+"F0.wireOp",EDGE,"ad75a4ee-e5a6-4fa7-b8b8-94f4a8825bbc.filletArc"),sQuery(id+"F0.wireOp",EDGE,"6ff16504-1f9c-458d-bf07-aac5f5830d14.filletArc"),sQuery(id+"F0.wireOp",EDGE,"b49fe1c4-a771-4eee-9138-79ecde32758b.filletArc"),sQuery(id+"F0.wireOp",EDGE,"E8.filletArc"),sQuery(id+"F0.wireOp",EDGE,"780f9540-5b47-44f2-a996-e532c960a919.filletArc")])]});
            hole(context, id + "F16", {"style" : HoleStyle.SIMPLE, "endStyle" : HoleEndStyle.BLIND, "holeDiameter" : 6 * mm, "holeDepth" : 2 * mm, "tappedDepth" : 12 * mm, "tapClearance" : 3, "locations" : qUnion([Q0, Q1]), "scope" : qUnion([Q2])});
        }
        {
            var Q0;
            Q0=sQuery(id+"F6.wireOp",VERTEX,"E56");
            var Q1;
            Q1=sQuery(id+"F6.wireOp",VERTEX,"E57");
            var Q2;
            Q2=makeQuery(id+"F1.opExtrude","SWEPT_BODY",BODY,{"disambiguationData":[OSD([sQuery(id+"F0.wireOp",EDGE,"E0.0"),sQuery(id+"F0.wireOp",EDGE,"E0.1"),sQuery(id+"F0.wireOp",EDGE,"E0.2"),sQuery(id+"F0.wireOp",EDGE,"E0.3"),sQuery(id+"F0.wireOp",EDGE,"E0.4"),sQuery(id+"F0.wireOp",EDGE,"E0.5"),sQuery(id+"F0.wireOp",EDGE,"E1.0"),sQuery(id+"F0.wireOp",EDGE,"E1.1"),sQuery(id+"F0.wireOp",EDGE,"E1.2"),sQuery(id+"F0.wireOp",EDGE,"E1.3"),sQuery(id+"F0.wireOp",EDGE,"E1.4"),sQuery(id+"F0.wireOp",EDGE,"E1.5"),sQuery(id+"F0.wireOp",EDGE,"qtYv5Qlg-lz4s-kEUD-Om88-7lSdra8USrlq"),sQuery(id+"F0.wireOp",EDGE,"2QYJyqNU-itui-Txcm-ziau-iXFr887Gd9CH"),sQuery(id+"F0.wireOp",EDGE,"YySKseKW-3tVR-XM2i-sfbE-A3hUb2wOsWk8"),sQuery(id+"F0.wireOp",EDGE,"Lxbxjq0N-10Ww-tbja-2Tz2-jBNBnu8PBPbP"),sQuery(id+"F0.wireOp",EDGE,"vIwuUKl2-2Kem-1Jnu-9PgQ-0QrErVIrz4Um"),sQuery(id+"F0.wireOp",EDGE,"fKHDwvwM-en0X-JEBE-N4jP-jXe72wWVmmUP"),sQuery(id+"F0.wireOp",EDGE,"E2.filletArc"),sQuery(id+"F0.wireOp",EDGE,"E3.filletArc"),sQuery(id+"F0.wireOp",EDGE,"E4.filletArc"),sQuery(id+"F0.wireOp",EDGE,"E5.filletArc"),sQuery(id+"F0.wireOp",EDGE,"E6.filletArc"),sQuery(id+"F0.wireOp",EDGE,"f75670f9-2a15-46ef-bb35-30587241fc96.filletArc"),sQuery(id+"F0.wireOp",EDGE,"c95b92e2-db18-4474-b396-5f44c590ad15.filletArc"),sQuery(id+"F0.wireOp",EDGE,"f16d8751-d18c-4831-acbc-1a13bea7c6bc.filletArc"),sQuery(id+"F0.wireOp",EDGE,"ea1bd330-e894-4266-8a44-9dcd888b044d.filletArc"),sQuery(id+"F0.wireOp",EDGE,"E7"),sQuery(id+"F0.wireOp",EDGE,"mCzg0sP5-OklU-KqC0-8pOI-dyTgrQixTGRZ"),sQuery(id+"F0.wireOp",EDGE,"WcAi2qTU-oJVa-IYYN-hlim-nuIIgn7LXuB4"),sQuery(id+"F0.wireOp",EDGE,"d29a9537-46ff-4a88-b732-ec67f0ea45bd.filletArc"),sQuery(id+"F0.wireOp",EDGE,"ad75a4ee-e5a6-4fa7-b8b8-94f4a8825bbc.filletArc"),sQuery(id+"F0.wireOp",EDGE,"6ff16504-1f9c-458d-bf07-aac5f5830d14.filletArc"),sQuery(id+"F0.wireOp",EDGE,"b49fe1c4-a771-4eee-9138-79ecde32758b.filletArc"),sQuery(id+"F0.wireOp",EDGE,"E8.filletArc"),sQuery(id+"F0.wireOp",EDGE,"780f9540-5b47-44f2-a996-e532c960a919.filletArc")])]});
            hole(context, id + "F17", {"style" : HoleStyle.SIMPLE, "endStyle" : HoleEndStyle.BLIND, "holeDiameter" : 6 * mm, "holeDepth" : 2 * mm, "tappedDepth" : 12 * mm, "tapClearance" : 3, "locations" : qUnion([Q0, Q1]), "scope" : qUnion([Q2])});
        }
        {
            var Q0;
            Q0=sQuery(id+"F6.wireOp",VERTEX,"E56");
            var Q1;
            Q1=sQuery(id+"F6.wireOp",VERTEX,"E57");
            var Q2;
            Q2=makeQuery(id+"F1.opExtrude","SWEPT_BODY",BODY,{"disambiguationData":[OSD([sQuery(id+"F0.wireOp",EDGE,"E0.0"),sQuery(id+"F0.wireOp",EDGE,"E0.1"),sQuery(id+"F0.wireOp",EDGE,"E0.2"),sQuery(id+"F0.wireOp",EDGE,"E0.3"),sQuery(id+"F0.wireOp",EDGE,"E0.4"),sQuery(id+"F0.wireOp",EDGE,"E0.5"),sQuery(id+"F0.wireOp",EDGE,"E1.0"),sQuery(id+"F0.wireOp",EDGE,"E1.1"),sQuery(id+"F0.wireOp",EDGE,"E1.2"),sQuery(id+"F0.wireOp",EDGE,"E1.3"),sQuery(id+"F0.wireOp",EDGE,"E1.4"),sQuery(id+"F0.wireOp",EDGE,"E1.5"),sQuery(id+"F0.wireOp",EDGE,"qtYv5Qlg-lz4s-kEUD-Om88-7lSdra8USrlq"),sQuery(id+"F0.wireOp",EDGE,"2QYJyqNU-itui-Txcm-ziau-iXFr887Gd9CH"),sQuery(id+"F0.wireOp",EDGE,"YySKseKW-3tVR-XM2i-sfbE-A3hUb2wOsWk8"),sQuery(id+"F0.wireOp",EDGE,"Lxbxjq0N-10Ww-tbja-2Tz2-jBNBnu8PBPbP"),sQuery(id+"F0.wireOp",EDGE,"vIwuUKl2-2Kem-1Jnu-9PgQ-0QrErVIrz4Um"),sQuery(id+"F0.wireOp",EDGE,"fKHDwvwM-en0X-JEBE-N4jP-jXe72wWVmmUP"),sQuery(id+"F0.wireOp",EDGE,"E2.filletArc"),sQuery(id+"F0.wireOp",EDGE,"E3.filletArc"),sQuery(id+"F0.wireOp",EDGE,"E4.filletArc"),sQuery(id+"F0.wireOp",EDGE,"E5.filletArc"),sQuery(id+"F0.wireOp",EDGE,"E6.filletArc"),sQuery(id+"F0.wireOp",EDGE,"f75670f9-2a15-46ef-bb35-30587241fc96.filletArc"),sQuery(id+"F0.wireOp",EDGE,"c95b92e2-db18-4474-b396-5f44c590ad15.filletArc"),sQuery(id+"F0.wireOp",EDGE,"f16d8751-d18c-4831-acbc-1a13bea7c6bc.filletArc"),sQuery(id+"F0.wireOp",EDGE,"ea1bd330-e894-4266-8a44-9dcd888b044d.filletArc"),sQuery(id+"F0.wireOp",EDGE,"E7"),sQuery(id+"F0.wireOp",EDGE,"mCzg0sP5-OklU-KqC0-8pOI-dyTgrQixTGRZ"),sQuery(id+"F0.wireOp",EDGE,"WcAi2qTU-oJVa-IYYN-hlim-nuIIgn7LXuB4"),sQuery(id+"F0.wireOp",EDGE,"d29a9537-46ff-4a88-b732-ec67f0ea45bd.filletArc"),sQuery(id+"F0.wireOp",EDGE,"ad75a4ee-e5a6-4fa7-b8b8-94f4a8825bbc.filletArc"),sQuery(id+"F0.wireOp",EDGE,"6ff16504-1f9c-458d-bf07-aac5f5830d14.filletArc"),sQuery(id+"F0.wireOp",EDGE,"b49fe1c4-a771-4eee-9138-79ecde32758b.filletArc"),sQuery(id+"F0.wireOp",EDGE,"E8.filletArc"),sQuery(id+"F0.wireOp",EDGE,"780f9540-5b47-44f2-a996-e532c960a919.filletArc")])]});
            hole(context, id + "F18", {"style" : HoleStyle.SIMPLE, "endStyle" : HoleEndStyle.BLIND, "standardTappedOrClearance" : lookupTablePath({ "standard" : "ISO", "fit" : "Normal", "size" : "M3", "type" : "Clearance" }), "standardBlindInLast" : lookupTablePath({ "fit" : "Standard", "standard" : "ISO", "size" : "M3", "type" : "Clearance" }), "holeDiameter" : 3.3 * mm, "holeDepth" : 13.5 * mm, "tappedDepth" : 12 * mm, "tapClearance" : 3, "locations" : qUnion([Q0, Q1]), "scope" : qUnion([Q2])});
        }
        {
            var Q0;
            Q0=sQuery(id+"F7.wireOp",VERTEX,"E58");
            var Q1;
            Q1=sQuery(id+"F7.wireOp",VERTEX,"E59");
            var Q2;
            Q2=makeQuery(id+"F1.opExtrude","SWEPT_BODY",BODY,{"disambiguationData":[OSD([sQuery(id+"F0.wireOp",EDGE,"E0.0"),sQuery(id+"F0.wireOp",EDGE,"E0.1"),sQuery(id+"F0.wireOp",EDGE,"E0.2"),sQuery(id+"F0.wireOp",EDGE,"E0.3"),sQuery(id+"F0.wireOp",EDGE,"E0.4"),sQuery(id+"F0.wireOp",EDGE,"E0.5"),sQuery(id+"F0.wireOp",EDGE,"E1.0"),sQuery(id+"F0.wireOp",EDGE,"E1.1"),sQuery(id+"F0.wireOp",EDGE,"E1.2"),sQuery(id+"F0.wireOp",EDGE,"E1.3"),sQuery(id+"F0.wireOp",EDGE,"E1.4"),sQuery(id+"F0.wireOp",EDGE,"E1.5"),sQuery(id+"F0.wireOp",EDGE,"qtYv5Qlg-lz4s-kEUD-Om88-7lSdra8USrlq"),sQuery(id+"F0.wireOp",EDGE,"2QYJyqNU-itui-Txcm-ziau-iXFr887Gd9CH"),sQuery(id+"F0.wireOp",EDGE,"YySKseKW-3tVR-XM2i-sfbE-A3hUb2wOsWk8"),sQuery(id+"F0.wireOp",EDGE,"Lxbxjq0N-10Ww-tbja-2Tz2-jBNBnu8PBPbP"),sQuery(id+"F0.wireOp",EDGE,"vIwuUKl2-2Kem-1Jnu-9PgQ-0QrErVIrz4Um"),sQuery(id+"F0.wireOp",EDGE,"fKHDwvwM-en0X-JEBE-N4jP-jXe72wWVmmUP"),sQuery(id+"F0.wireOp",EDGE,"E2.filletArc"),sQuery(id+"F0.wireOp",EDGE,"E3.filletArc"),sQuery(id+"F0.wireOp",EDGE,"E4.filletArc"),sQuery(id+"F0.wireOp",EDGE,"E5.filletArc"),sQuery(id+"F0.wireOp",EDGE,"E6.filletArc"),sQuery(id+"F0.wireOp",EDGE,"f75670f9-2a15-46ef-bb35-30587241fc96.filletArc"),sQuery(id+"F0.wireOp",EDGE,"c95b92e2-db18-4474-b396-5f44c590ad15.filletArc"),sQuery(id+"F0.wireOp",EDGE,"f16d8751-d18c-4831-acbc-1a13bea7c6bc.filletArc"),sQuery(id+"F0.wireOp",EDGE,"ea1bd330-e894-4266-8a44-9dcd888b044d.filletArc"),sQuery(id+"F0.wireOp",EDGE,"E7"),sQuery(id+"F0.wireOp",EDGE,"mCzg0sP5-OklU-KqC0-8pOI-dyTgrQixTGRZ"),sQuery(id+"F0.wireOp",EDGE,"WcAi2qTU-oJVa-IYYN-hlim-nuIIgn7LXuB4"),sQuery(id+"F0.wireOp",EDGE,"d29a9537-46ff-4a88-b732-ec67f0ea45bd.filletArc"),sQuery(id+"F0.wireOp",EDGE,"ad75a4ee-e5a6-4fa7-b8b8-94f4a8825bbc.filletArc"),sQuery(id+"F0.wireOp",EDGE,"6ff16504-1f9c-458d-bf07-aac5f5830d14.filletArc"),sQuery(id+"F0.wireOp",EDGE,"b49fe1c4-a771-4eee-9138-79ecde32758b.filletArc"),sQuery(id+"F0.wireOp",EDGE,"E8.filletArc"),sQuery(id+"F0.wireOp",EDGE,"780f9540-5b47-44f2-a996-e532c960a919.filletArc")])]});
            hole(context, id + "F19", {"style" : HoleStyle.SIMPLE, "endStyle" : HoleEndStyle.BLIND, "standardTappedOrClearance" : lookupTablePath({ "standard" : "ISO", "fit" : "Normal", "size" : "M3", "type" : "Clearance" }), "standardBlindInLast" : lookupTablePath({ "fit" : "Standard", "standard" : "ISO", "size" : "M3", "type" : "Clearance" }), "holeDiameter" : 3.3 * mm, "holeDepth" : 13.5 * mm, "tappedDepth" : 12 * mm, "tapClearance" : 3, "locations" : qUnion([Q0, Q1]), "scope" : qUnion([Q2])});
        }
        {
            var Q0;
            Q0=sQuery(id+"F7.wireOp",VERTEX,"E58");
            var Q1;
            Q1=sQuery(id+"F7.wireOp",VERTEX,"E59");
            var Q2;
            Q2=makeQuery(id+"F1.opExtrude","SWEPT_BODY",BODY,{"disambiguationData":[OSD([sQuery(id+"F0.wireOp",EDGE,"E0.0"),sQuery(id+"F0.wireOp",EDGE,"E0.1"),sQuery(id+"F0.wireOp",EDGE,"E0.2"),sQuery(id+"F0.wireOp",EDGE,"E0.3"),sQuery(id+"F0.wireOp",EDGE,"E0.4"),sQuery(id+"F0.wireOp",EDGE,"E0.5"),sQuery(id+"F0.wireOp",EDGE,"E1.0"),sQuery(id+"F0.wireOp",EDGE,"E1.1"),sQuery(id+"F0.wireOp",EDGE,"E1.2"),sQuery(id+"F0.wireOp",EDGE,"E1.3"),sQuery(id+"F0.wireOp",EDGE,"E1.4"),sQuery(id+"F0.wireOp",EDGE,"E1.5"),sQuery(id+"F0.wireOp",EDGE,"qtYv5Qlg-lz4s-kEUD-Om88-7lSdra8USrlq"),sQuery(id+"F0.wireOp",EDGE,"2QYJyqNU-itui-Txcm-ziau-iXFr887Gd9CH"),sQuery(id+"F0.wireOp",EDGE,"YySKseKW-3tVR-XM2i-sfbE-A3hUb2wOsWk8"),sQuery(id+"F0.wireOp",EDGE,"Lxbxjq0N-10Ww-tbja-2Tz2-jBNBnu8PBPbP"),sQuery(id+"F0.wireOp",EDGE,"vIwuUKl2-2Kem-1Jnu-9PgQ-0QrErVIrz4Um"),sQuery(id+"F0.wireOp",EDGE,"fKHDwvwM-en0X-JEBE-N4jP-jXe72wWVmmUP"),sQuery(id+"F0.wireOp",EDGE,"E2.filletArc"),sQuery(id+"F0.wireOp",EDGE,"E3.filletArc"),sQuery(id+"F0.wireOp",EDGE,"E4.filletArc"),sQuery(id+"F0.wireOp",EDGE,"E5.filletArc"),sQuery(id+"F0.wireOp",EDGE,"E6.filletArc"),sQuery(id+"F0.wireOp",EDGE,"f75670f9-2a15-46ef-bb35-30587241fc96.filletArc"),sQuery(id+"F0.wireOp",EDGE,"c95b92e2-db18-4474-b396-5f44c590ad15.filletArc"),sQuery(id+"F0.wireOp",EDGE,"f16d8751-d18c-4831-acbc-1a13bea7c6bc.filletArc"),sQuery(id+"F0.wireOp",EDGE,"ea1bd330-e894-4266-8a44-9dcd888b044d.filletArc"),sQuery(id+"F0.wireOp",EDGE,"E7"),sQuery(id+"F0.wireOp",EDGE,"mCzg0sP5-OklU-KqC0-8pOI-dyTgrQixTGRZ"),sQuery(id+"F0.wireOp",EDGE,"WcAi2qTU-oJVa-IYYN-hlim-nuIIgn7LXuB4"),sQuery(id+"F0.wireOp",EDGE,"d29a9537-46ff-4a88-b732-ec67f0ea45bd.filletArc"),sQuery(id+"F0.wireOp",EDGE,"ad75a4ee-e5a6-4fa7-b8b8-94f4a8825bbc.filletArc"),sQuery(id+"F0.wireOp",EDGE,"6ff16504-1f9c-458d-bf07-aac5f5830d14.filletArc"),sQuery(id+"F0.wireOp",EDGE,"b49fe1c4-a771-4eee-9138-79ecde32758b.filletArc"),sQuery(id+"F0.wireOp",EDGE,"E8.filletArc"),sQuery(id+"F0.wireOp",EDGE,"780f9540-5b47-44f2-a996-e532c960a919.filletArc")])]});
            hole(context, id + "F20", {"style" : HoleStyle.SIMPLE, "endStyle" : HoleEndStyle.BLIND, "holeDiameter" : 6 * mm, "holeDepth" : 2 * mm, "tappedDepth" : 12 * mm, "tapClearance" : 3, "locations" : qUnion([Q0, Q1]), "scope" : qUnion([Q2])});
        }
        {
            var Q0;
            {var subQ0=sQuery(id+"F0.wireOp",EDGE,"E46");Q0=makeQuery(id+"F2.boolean.opBoolean","MERGE",FACE,{"derivedFrom":[makeQuery(id+"F1.opExtrude","SWEPT_FACE",FACE,{"disambiguationData":[OSD([subQ0])]}),makeQuery(id+"F2.opExtrude","SWEPT_FACE",FACE,{"disambiguationData":[OSD([subQ0])]})]});}
            var sketch = newSketch(context, id + "F21", { "sketchPlane" : qUnion([Q0])});
            skCircle(sketch, "E62.cCircle", {"center": v(5, 8.5) * mm, "radius": 2.9 * mm, "construction": true});
            skLineSegment(sketch, "E62.0", {"start": v(7.9, 6.83) * mm, "end": v(5, 5.15) * mm});
            skLineSegment(sketch, "E62.1", {"start": v(5, 5.15) * mm, "end": v(2.1, 6.83) * mm});
            skLineSegment(sketch, "E62.2", {"start": v(2.1, 6.83) * mm, "end": v(2.1, 10.17) * mm});
            skLineSegment(sketch, "E62.3", {"start": v(2.1, 10.17) * mm, "end": v(5, 11.85) * mm});
            skLineSegment(sketch, "E62.4", {"start": v(5, 11.85) * mm, "end": v(7.9, 10.17) * mm});
            skLineSegment(sketch, "E62.5", {"start": v(7.9, 10.17) * mm, "end": v(7.9, 6.83) * mm});
            skPoint(sketch, "E62.0.midPoint", {"position": v(6.45, 5.99) * mm});
            skCircle(sketch, "E63.cCircle", {"center": v(5, -8.5) * mm, "radius": 2.9 * mm, "construction": true});
            skLineSegment(sketch, "E63.0", {"start": v(5, -11.85) * mm, "end": v(2.1, -10.17) * mm});
            skLineSegment(sketch, "E63.1", {"start": v(2.1, -10.17) * mm, "end": v(2.1, -6.83) * mm});
            skLineSegment(sketch, "E63.2", {"start": v(2.1, -6.83) * mm, "end": v(5, -5.15) * mm});
            skLineSegment(sketch, "E63.3", {"start": v(5, -5.15) * mm, "end": v(7.9, -6.83) * mm});
            skLineSegment(sketch, "E63.4", {"start": v(7.9, -6.83) * mm, "end": v(7.9, -10.17) * mm});
            skLineSegment(sketch, "E63.5", {"start": v(7.9, -10.17) * mm, "end": v(5, -11.85) * mm});
            skPoint(sketch, "E63.0.midPoint", {"position": v(3.55, -11.01) * mm});
            skSolve(sketch);
        }
        {
            var Q0;
            Q0 = qSketchRegion(id + "F21", true);
            extrude(context, id + "F22", {"entities" : qUnion([Q0]), "operationType" : NewBodyOperationType.REMOVE, "oppositeDirection" : true, "depth" : 2 * mm});
        }
        {
            var Q0;
            {var subQ0=sQuery(id+"F0.wireOp",EDGE,"E1.4");Q0=makeQuery(id+"F2.boolean.opBoolean","MERGE",FACE,{"derivedFrom":[makeQuery(id+"F1.opExtrude","SWEPT_FACE",FACE,{"disambiguationData":[OSD([subQ0])]}),makeQuery(id+"F2.opExtrude","SWEPT_FACE",FACE,{"disambiguationData":[OSD([subQ0])]})]});}
            var sketch = newSketch(context, id + "F23", { "sketchPlane" : qUnion([Q0])});
            skPoint(sketch, "E64.0.midPoint", {"position": v(-7.5, 10) * mm});
            skCircle(sketch, "E65.cCircle", {"center": v(8.5, 5) * mm, "radius": 2.9 * mm, "construction": true});
            skLineSegment(sketch, "E65.0", {"start": v(6.83, 7.9) * mm, "end": v(10.17, 7.9) * mm});
            skLineSegment(sketch, "E65.1", {"start": v(10.17, 7.9) * mm, "end": v(11.85, 5) * mm});
            skLineSegment(sketch, "E65.2", {"start": v(11.85, 5) * mm, "end": v(10.17, 2.1) * mm});
            skLineSegment(sketch, "E65.3", {"start": v(10.17, 2.1) * mm, "end": v(6.83, 2.1) * mm});
            skLineSegment(sketch, "E65.4", {"start": v(6.83, 2.1) * mm, "end": v(5.15, 5) * mm});
            skLineSegment(sketch, "E65.5", {"start": v(5.15, 5) * mm, "end": v(6.83, 7.9) * mm});
            skPoint(sketch, "E65.0.midPoint", {"position": v(8.5, 7.9) * mm});
            skCircle(sketch, "E66.cCircle", {"center": v(-8.5, 5) * mm, "radius": 2.9 * mm, "construction": true});
            skLineSegment(sketch, "E66.0", {"start": v(-10.17, 7.9) * mm, "end": v(-6.83, 7.9) * mm});
            skLineSegment(sketch, "E66.1", {"start": v(-6.83, 7.9) * mm, "end": v(-5.15, 5) * mm});
            skLineSegment(sketch, "E66.2", {"start": v(-5.15, 5) * mm, "end": v(-6.83, 2.1) * mm});
            skLineSegment(sketch, "E66.3", {"start": v(-6.83, 2.1) * mm, "end": v(-10.17, 2.1) * mm});
            skLineSegment(sketch, "E66.4", {"start": v(-10.17, 2.1) * mm, "end": v(-11.85, 5) * mm});
            skLineSegment(sketch, "E66.5", {"start": v(-11.85, 5) * mm, "end": v(-10.17, 7.9) * mm});
            skPoint(sketch, "E66.0.midPoint", {"position": v(-8.5, 7.9) * mm});
            skSolve(sketch);
        }
        {
            var Q0;
            Q0 = qSketchRegion(id + "F23", true);
            extrude(context, id + "F24", {"entities" : qUnion([Q0]), "operationType" : NewBodyOperationType.REMOVE, "oppositeDirection" : true, "depth" : 2 * mm});
        }
        {
            var Q0;
            {var subQ0=sQuery(id+"F0.wireOp",EDGE,"E1.3");Q0=makeQuery(id+"F2.boolean.opBoolean","MERGE",FACE,{"derivedFrom":[makeQuery(id+"F1.opExtrude","SWEPT_FACE",FACE,{"disambiguationData":[OSD([subQ0])]}),makeQuery(id+"F2.opExtrude","SWEPT_FACE",FACE,{"disambiguationData":[OSD([subQ0])]})]});}
            var sketch = newSketch(context, id + "F25", { "sketchPlane" : qUnion([Q0])});
            skCircle(sketch, "E67.cCircle", {"center": v(-5, 8.5) * mm, "radius": 2.9 * mm, "construction": true});
            skLineSegment(sketch, "E67.0", {"start": v(-7.9, 10.19) * mm, "end": v(-4.98, 11.85) * mm});
            skLineSegment(sketch, "E67.1", {"start": v(-4.98, 11.85) * mm, "end": v(-2.1, 10.16) * mm});
            skLineSegment(sketch, "E67.2", {"start": v(-2.1, 10.16) * mm, "end": v(-2.1, 6.81) * mm});
            skLineSegment(sketch, "E67.3", {"start": v(-2.1, 6.81) * mm, "end": v(-5.02, 5.15) * mm});
            skLineSegment(sketch, "E67.4", {"start": v(-5.02, 5.15) * mm, "end": v(-7.9, 6.84) * mm});
            skLineSegment(sketch, "E67.5", {"start": v(-7.9, 6.84) * mm, "end": v(-7.9, 10.19) * mm});
            skPoint(sketch, "E67.0.midPoint", {"position": v(-6.44, 11.02) * mm});
            skSolve(sketch);
        }
        {
            var Q0;
            Q0=makeQuery(id+"F25.imprint","IMPRINT",FACE,{"disambiguationData":[TD([[makeQuery(id+"F25.imprint","IMPRINT",EDGE,{"derivedFrom":sQuery(id+"F25.wireOp",EDGE,"E67.0")}),-1.0]])]});
            extrude(context, id + "F26", {"entities" : qUnion([Q0]), "operationType" : NewBodyOperationType.REMOVE, "oppositeDirection" : true, "depth" : 2 * mm});
        }
        {
            var Q0;
            {var subQ0=sQuery(id+"F0.wireOp",EDGE,"E10");Q0=makeQuery(id+"F2.boolean.opBoolean","MERGE",FACE,{"derivedFrom":[makeQuery(id+"F1.opExtrude","SWEPT_FACE",FACE,{"disambiguationData":[OSD([subQ0])]}),makeQuery(id+"F2.opExtrude","SWEPT_FACE",FACE,{"disambiguationData":[OSD([subQ0])]})]});}
            var sketch = newSketch(context, id + "F27", { "sketchPlane" : qUnion([Q0])});
            skCircle(sketch, "E68.cCircle", {"center": v(-5, -8.33) * mm, "radius": 2.9 * mm, "construction": true});
            skLineSegment(sketch, "E68.0", {"start": v(-7.9, -10) * mm, "end": v(-7.9, -6.66) * mm});
            skLineSegment(sketch, "E68.1", {"start": v(-7.9, -6.66) * mm, "end": v(-5, -4.98) * mm});
            skLineSegment(sketch, "E68.2", {"start": v(-5, -4.98) * mm, "end": v(-2.1, -6.66) * mm});
            skLineSegment(sketch, "E68.3", {"start": v(-2.1, -6.66) * mm, "end": v(-2.1, -10) * mm});
            skLineSegment(sketch, "E68.4", {"start": v(-2.1, -10) * mm, "end": v(-5, -11.68) * mm});
            skLineSegment(sketch, "E68.5", {"start": v(-5, -11.68) * mm, "end": v(-7.9, -10) * mm});
            skPoint(sketch, "E68.0.midPoint", {"position": v(-7.9, -8.33) * mm});
            skSolve(sketch);
        }
        {
            var Q0;
            Q0 = qSketchRegion(id + "F27", true);
            extrude(context, id + "F28", {"entities" : qUnion([Q0]), "operationType" : NewBodyOperationType.REMOVE, "oppositeDirection" : true, "depth" : 2 * mm});
        }
        {
            var Q0;
            {var subQ0=sQuery(id+"F0.wireOp",EDGE,"E1.2");Q0=makeQuery(id+"F2.boolean.opBoolean","MERGE",FACE,{"derivedFrom":[makeQuery(id+"F1.opExtrude","SWEPT_FACE",FACE,{"disambiguationData":[OSD([subQ0])]}),makeQuery(id+"F2.opExtrude","SWEPT_FACE",FACE,{"disambiguationData":[OSD([subQ0])]})]});}
            var sketch = newSketch(context, id + "F29", { "sketchPlane" : qUnion([Q0])});
            skCircle(sketch, "E69.cCircle", {"center": v(-5, -8.5) * mm, "radius": 2.9 * mm, "construction": true});
            skLineSegment(sketch, "E69.0", {"start": v(-7.9, -10.17) * mm, "end": v(-7.9, -6.83) * mm});
            skLineSegment(sketch, "E69.1", {"start": v(-7.9, -6.83) * mm, "end": v(-5, -5.15) * mm});
            skLineSegment(sketch, "E69.2", {"start": v(-5, -5.15) * mm, "end": v(-2.1, -6.83) * mm});
            skLineSegment(sketch, "E69.3", {"start": v(-2.1, -6.83) * mm, "end": v(-2.1, -10.17) * mm});
            skLineSegment(sketch, "E69.4", {"start": v(-2.1, -10.17) * mm, "end": v(-5, -11.85) * mm});
            skLineSegment(sketch, "E69.5", {"start": v(-5, -11.85) * mm, "end": v(-7.9, -10.17) * mm});
            skPoint(sketch, "E69.0.midPoint", {"position": v(-7.9, -8.5) * mm});
            skCircle(sketch, "E70.cCircle", {"center": v(-5, 8.5) * mm, "radius": 2.9 * mm, "construction": true});
            skLineSegment(sketch, "E70.0", {"start": v(-7.9, 6.83) * mm, "end": v(-7.9, 10.17) * mm});
            skLineSegment(sketch, "E70.1", {"start": v(-7.9, 10.17) * mm, "end": v(-5, 11.85) * mm});
            skLineSegment(sketch, "E70.2", {"start": v(-5, 11.85) * mm, "end": v(-2.1, 10.17) * mm});
            skLineSegment(sketch, "E70.3", {"start": v(-2.1, 10.17) * mm, "end": v(-2.1, 6.83) * mm});
            skLineSegment(sketch, "E70.4", {"start": v(-2.1, 6.83) * mm, "end": v(-5, 5.15) * mm});
            skLineSegment(sketch, "E70.5", {"start": v(-5, 5.15) * mm, "end": v(-7.9, 6.83) * mm});
            skPoint(sketch, "E70.0.midPoint", {"position": v(-7.9, 8.5) * mm});
            skSolve(sketch);
        }
        {
            var Q0;
            Q0=makeQuery(id+"F29.imprint","IMPRINT",FACE,{"disambiguationData":[TD([[makeQuery(id+"F29.imprint","IMPRINT",EDGE,{"derivedFrom":sQuery(id+"F29.wireOp",EDGE,"E69.0")}),-1.0]])]});
            var Q1;
            Q1=makeQuery(id+"F29.imprint","IMPRINT",FACE,{"disambiguationData":[TD([[makeQuery(id+"F29.imprint","IMPRINT",EDGE,{"derivedFrom":sQuery(id+"F29.wireOp",EDGE,"E70.0")}),-1.0]])]});
            extrude(context, id + "F30", {"entities" : qUnion([Q0, Q1]), "operationType" : NewBodyOperationType.REMOVE, "oppositeDirection" : true, "depth" : 2 * mm});
        }
        {
            var Q0;
            {var subQ0=sQuery(id+"F0.wireOp",EDGE,"E40");Q0=makeQuery(id+"F2.boolean.opBoolean","MERGE",FACE,{"derivedFrom":[makeQuery(id+"F1.opExtrude","SWEPT_FACE",FACE,{"disambiguationData":[OSD([subQ0])]}),makeQuery(id+"F2.opExtrude","SWEPT_FACE",FACE,{"disambiguationData":[OSD([subQ0])]})]});}
            var sketch = newSketch(context, id + "F31", { "sketchPlane" : qUnion([Q0])});
            skCircle(sketch, "E71.cCircle", {"center": v(8.37, -5) * mm, "radius": 2.9 * mm, "construction": true});
            skLineSegment(sketch, "E71.0", {"start": v(6.71, -7.9) * mm, "end": v(5.02, -5.01) * mm});
            skLineSegment(sketch, "E71.1", {"start": v(5.02, -5.01) * mm, "end": v(6.69, -2.1) * mm});
            skLineSegment(sketch, "E71.2", {"start": v(6.69, -2.1) * mm, "end": v(10.04, -2.1) * mm});
            skLineSegment(sketch, "E71.3", {"start": v(10.04, -2.1) * mm, "end": v(11.72, -4.99) * mm});
            skLineSegment(sketch, "E71.4", {"start": v(11.72, -4.99) * mm, "end": v(10.06, -7.9) * mm});
            skLineSegment(sketch, "E71.5", {"start": v(10.06, -7.9) * mm, "end": v(6.71, -7.9) * mm});
            skPoint(sketch, "E71.0.midPoint", {"position": v(5.87, -6.46) * mm});
            skCircle(sketch, "E72.cCircle", {"center": v(-8.63, -5) * mm, "radius": 2.9 * mm, "construction": true});
            skLineSegment(sketch, "E72.0", {"start": v(-6.95, -7.9) * mm, "end": v(-10.3, -7.9) * mm});
            skLineSegment(sketch, "E72.1", {"start": v(-10.3, -7.9) * mm, "end": v(-11.98, -5) * mm});
            skLineSegment(sketch, "E72.2", {"start": v(-11.98, -5) * mm, "end": v(-10.3, -2.1) * mm});
            skLineSegment(sketch, "E72.3", {"start": v(-10.3, -2.1) * mm, "end": v(-6.95, -2.1) * mm});
            skLineSegment(sketch, "E72.4", {"start": v(-6.95, -2.1) * mm, "end": v(-5.28, -5) * mm});
            skLineSegment(sketch, "E72.5", {"start": v(-5.28, -5) * mm, "end": v(-6.95, -7.9) * mm});
            skPoint(sketch, "E72.0.midPoint", {"position": v(-8.63, -7.9) * mm});
            skSolve(sketch);
        }
        {
            var Q0;
            Q0 = qSketchRegion(id + "F31", true);
            extrude(context, id + "F32", {"entities" : qUnion([Q0]), "operationType" : NewBodyOperationType.REMOVE, "oppositeDirection" : true, "depth" : 2 * mm});
        }
        {
            var Q0;
            {var subQ0=sQuery(id+"F0.wireOp",EDGE,"E11");Q0=makeQuery(id+"F2.boolean.opBoolean","MERGE",FACE,{"derivedFrom":[makeQuery(id+"F1.opExtrude","SWEPT_FACE",FACE,{"disambiguationData":[OSD([subQ0])]}),makeQuery(id+"F2.opExtrude","SWEPT_FACE",FACE,{"disambiguationData":[OSD([subQ0])]})]});}
            var sketch = newSketch(context, id + "F33", { "sketchPlane" : qUnion([Q0])});
            skCircle(sketch, "E73.cCircle", {"center": v(5, -8.67) * mm, "radius": 2.9 * mm, "construction": true});
            skLineSegment(sketch, "E73.0", {"start": v(7.9, -7) * mm, "end": v(7.9, -10.35) * mm});
            skLineSegment(sketch, "E73.1", {"start": v(7.9, -10.35) * mm, "end": v(5, -12.02) * mm});
            skLineSegment(sketch, "E73.2", {"start": v(5, -12.02) * mm, "end": v(2.1, -10.35) * mm});
            skLineSegment(sketch, "E73.3", {"start": v(2.1, -10.35) * mm, "end": v(2.1, -7) * mm});
            skLineSegment(sketch, "E73.4", {"start": v(2.1, -7) * mm, "end": v(5, -5.32) * mm});
            skLineSegment(sketch, "E73.5", {"start": v(5, -5.32) * mm, "end": v(7.9, -7) * mm});
            skPoint(sketch, "E73.0.midPoint", {"position": v(7.9, -8.67) * mm});
            skCircle(sketch, "E74.cCircle", {"center": v(5, 8.33) * mm, "radius": 2.9 * mm, "construction": true});
            skLineSegment(sketch, "E74.0", {"start": v(7.9, 10) * mm, "end": v(7.9, 6.66) * mm});
            skLineSegment(sketch, "E74.1", {"start": v(7.9, 6.66) * mm, "end": v(5, 4.98) * mm});
            skLineSegment(sketch, "E74.2", {"start": v(5, 4.98) * mm, "end": v(2.1, 6.66) * mm});
            skLineSegment(sketch, "E74.3", {"start": v(2.1, 6.66) * mm, "end": v(2.1, 10) * mm});
            skLineSegment(sketch, "E74.4", {"start": v(2.1, 10) * mm, "end": v(5, 11.68) * mm});
            skLineSegment(sketch, "E74.5", {"start": v(5, 11.68) * mm, "end": v(7.9, 10) * mm});
            skPoint(sketch, "E74.0.midPoint", {"position": v(7.9, 8.33) * mm});
            skSolve(sketch);
        }
        {
            var Q0;
            Q0 = qSketchRegion(id + "F33", true);
            extrude(context, id + "F34", {"entities" : qUnion([Q0]), "operationType" : NewBodyOperationType.REMOVE, "oppositeDirection" : true, "depth" : 2 * mm});
        }
        {
            var Q0;
            Q0=sQuery(id+"F0.wireOp",VERTEX,"E1.cCircle.center");
            var Q1;
            Q1=makeQuery(id+"F1.opExtrude","SWEPT_BODY",BODY,{"disambiguationData":[OSD([sQuery(id+"F0.wireOp",EDGE,"E0.0"),sQuery(id+"F0.wireOp",EDGE,"E0.1"),sQuery(id+"F0.wireOp",EDGE,"E0.2"),sQuery(id+"F0.wireOp",EDGE,"E0.3"),sQuery(id+"F0.wireOp",EDGE,"E0.4"),sQuery(id+"F0.wireOp",EDGE,"E0.5"),sQuery(id+"F0.wireOp",EDGE,"E1.2"),sQuery(id+"F0.wireOp",EDGE,"E1.3"),sQuery(id+"F0.wireOp",EDGE,"E1.4"),sQuery(id+"F0.wireOp",EDGE,"E7"),sQuery(id+"F0.wireOp",EDGE,"E10"),sQuery(id+"F0.wireOp",EDGE,"E11"),sQuery(id+"F0.wireOp",EDGE,"E14"),sQuery(id+"F0.wireOp",EDGE,"E15"),sQuery(id+"F0.wireOp",EDGE,"E16"),sQuery(id+"F0.wireOp",EDGE,"E17"),sQuery(id+"F0.wireOp",EDGE,"E18"),sQuery(id+"F0.wireOp",EDGE,"E19"),sQuery(id+"F0.wireOp",EDGE,"E20"),sQuery(id+"F0.wireOp",EDGE,"E21"),sQuery(id+"F0.wireOp",EDGE,"E22"),sQuery(id+"F0.wireOp",EDGE,"E23"),sQuery(id+"F0.wireOp",EDGE,"E24"),sQuery(id+"F0.wireOp",EDGE,"E25"),sQuery(id+"F0.wireOp",EDGE,"E26.filletArc"),sQuery(id+"F0.wireOp",EDGE,"E27.filletArc"),sQuery(id+"F0.wireOp",EDGE,"E28.filletArc"),sQuery(id+"F0.wireOp",EDGE,"E29.filletArc"),sQuery(id+"F0.wireOp",EDGE,"E30.filletArc"),sQuery(id+"F0.wireOp",EDGE,"E31.filletArc"),sQuery(id+"F0.wireOp",EDGE,"E32.filletArc"),sQuery(id+"F0.wireOp",EDGE,"E33.filletArc"),sQuery(id+"F0.wireOp",EDGE,"E34.filletArc"),sQuery(id+"F0.wireOp",EDGE,"E35.filletArc"),sQuery(id+"F0.wireOp",EDGE,"E36.filletArc"),sQuery(id+"F0.wireOp",EDGE,"E37.filletArc"),sQuery(id+"F0.wireOp",EDGE,"E39.filletArc"),sQuery(id+"F0.wireOp",EDGE,"E40"),sQuery(id+"F0.wireOp",EDGE,"E41.filletArc"),sQuery(id+"F0.wireOp",EDGE,"E42.filletArc"),sQuery(id+"F0.wireOp",EDGE,"E43.filletArc"),sQuery(id+"F0.wireOp",EDGE,"E44.filletArc"),sQuery(id+"F0.wireOp",EDGE,"E45.filletArc"),sQuery(id+"F0.wireOp",EDGE,"E46")])]});
            hole(context, id + "F35", {"style" : HoleStyle.SIMPLE, "endStyle" : HoleEndStyle.BLIND, "oppositeDirection" : true, "standardTappedOrClearance" : lookupTablePath({ "standard" : "ISO", "fit" : "Normal", "size" : "M5", "type" : "Clearance" }), "standardBlindInLast" : lookupTablePath({ "fit" : "Standard", "standard" : "ISO", "size" : "M5", "type" : "Clearance" }), "holeDiameter" : 5.5 * mm, "holeDepth" : 15.8 * mm, "tappedDepth" : 12 * mm, "tapClearance" : 3, "locations" : qUnion([Q0]), "scope" : qUnion([Q1])});
        }
    });
